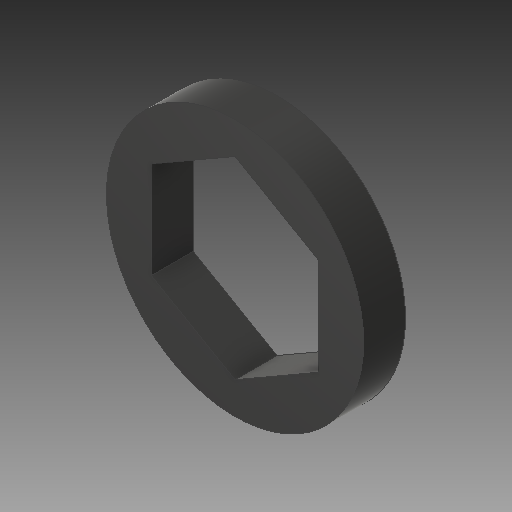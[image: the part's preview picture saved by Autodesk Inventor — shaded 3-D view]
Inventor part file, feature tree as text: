
AUTODESK INVENTOR PART (.ipt)
format: ipt  version: 2019 (Build 230136000, 136)  size: 97,280 bytes
history: native  units: in
note: dims shown in document units (in); Inventor stores cm internally (conversion verified against a paired STEP export)
features: extrude x1, sketch x1
ambient origin geometry x8: Origin, YZ Plane, XZ Plane, XY Plane, X Axis, Y Axis, Z Axis, Center Point
bodies: Solid1 (feature_tree)
feature tree (2):
  extrude  "Extrusion1"  Depth=0.125in
  sketch  "Sketch1"  dims[d0=0.5in d1=0.768in d2=0.125in d3=0.0in]
